FREECAD ASSEMBLY — COMPONENT RECIPES ("roommake")

This assembly document has 24 components, labeled P0..P23 below (a component is one placed body or linked part). 22 of them carry a construction recipe — the FreeCAD feature program that regenerates the part from scratch, quoted from this document or its linked companion documents; the rest are supplied as boundary geometry only. No exploded tour is included for this assembly.
NOTE — document 3 of 3 of this assembly tour. The two overview renders and the header above are repeated from document 1; the component sections below continue where the previous document stopped.
COMPONENT P19 — recipe-attached ("tv", a linked part whose construction recipe lives in a companion FreeCAD document of the same project; that document's serialized recipe follows).
Construction recipe (the companion document, serialized — sketch geometry with constraints, then the solid features built on it; lengths are millimeters unless a unit is written):

FCSTD DOCUMENT  (FreeCAD 1.0R39109 (Git))
Label: tv
License: All rights reserved
LicenseURL: https://en.wikipedia.org/wiki/All_rights_reserved
objects: Sketcher::SketchObject×9, PartDesign::Pad×6, PartDesign::Pocket×3, PartDesign::Body×3, App::Link×3, PartDesign::Fillet×2, Assembly::JointGroup×2, Assembly::AssemblyObject×2, Part::FeaturePython×2, PartDesign::ShapeBinder×2, PartDesign::Plane×2, App::Part×1
note: 60 computed .brp shape members not serialized (recipe doc carries the construction recipe); baked Part::Feature solids carry a one-line shape summary decoded from their .brp

FEATURE [Sketcher::SketchObject] Sketch003
  ArcFitTolerance = 1e-06
  AttachmentSupport = -> [XZ_Plane]
  FullyConstrained = true
  MakeInternals = false
  MapMode = 5
  Placement = pos=(0,0,0) rot=(1,0,0;1.5708rad)
  sketch-geometry (5):
    g0: LineSegment StartX=-4820 StartY=820 StartZ=0 EndX=4820 EndY=820 EndZ=0
    g1: LineSegment StartX=4820 StartY=820 StartZ=0 EndX=4820 EndY=6290 EndZ=0
    g2: LineSegment StartX=4820 StartY=6290 StartZ=0 EndX=-4820 EndY=6290 EndZ=0
    g3: LineSegment StartX=-4820 StartY=6290 StartZ=0 EndX=-4820 EndY=820 EndZ=0
    g4: GeomPoint [constr] X=0 Y=3555 Z=0
  constraints (13):
    c: Coincident(g0,g1)
    c: Coincident(g1,g2)
    c: Coincident(g2,g3)
    c: Coincident(g3,g0)
    c: Horizontal(g0)
    c: Horizontal(g2)
    c: Vertical(g1)
    c: Vertical(g3)
    c: Symmetric(g2,g0,g4)
    c: Distance(g1,g3) = 9640
    c: PointOnObject(g4,g-2)
    c: DistanceY(g1,g1) = 5470
    c: DistanceY(g0) = 820
FEATURE [PartDesign::Pad] Pad
  Direction = (0,-1,2e-16)
  Length = 100
  Length2 = 10
  Placement = pos=(0,0,0) rot=(1,0,0;1.5708rad)
  Profile = -> Sketch003
  ReferenceAxis = -> Sketch003 [N_Axis]
  Refine = true
  Suppressed = false
  Type = 0
FEATURE [Sketcher::SketchObject] Sketch004
  ArcFitTolerance = 1e-06
  AttachmentSupport = -> [Pad]
  ExternalGeometry = -> [Pad]
  FullyConstrained = true
  MakeInternals = false
  MapMode = 5
  Placement = pos=(0,7.894e-13,0) rot=(-1,0,0;1.5708rad)
  sketch-geometry (4):
    g0: LineSegment StartX=-4820 StartY=-820 StartZ=0 EndX=-4820 EndY=-1620 EndZ=0
    g1: LineSegment StartX=-4820 StartY=-1620 StartZ=0 EndX=4820 EndY=-1620 EndZ=0
    g2: LineSegment StartX=4820 StartY=-1620 StartZ=0 EndX=4820 EndY=-820 EndZ=0
    g3: LineSegment StartX=4820 StartY=-820 StartZ=0 EndX=-4820 EndY=-820 EndZ=0
  constraints (10):
    c: Coincident(g0,g1)
    c: Coincident(g1,g2)
    c: Coincident(g2,g3)
    c: Coincident(g3,g0)
    c: Vertical(g0)
    c: Vertical(g2)
    c: Horizontal(g1)
    c: DistanceY(g0,g0) = 800
    c: Coincident(g2,g-3)
    c: Coincident(g0,g-4)
FEATURE [PartDesign::Pad] Pad001
  BaseFeature = -> Pad
  Direction = (0,1,2e-16)
  Length = 800
  Length2 = 10
  Placement = pos=(0,0,0) rot=(1,0,0;1.5708rad)
  Profile = -> Sketch004
  ReferenceAxis = -> Sketch004 [N_Axis]
  Refine = true
  Suppressed = false
  Type = 0
FEATURE [Sketcher::SketchObject] Sketch005
  ArcFitTolerance = 1e-06
  AttachmentSupport = -> [Pad001]
  ExternalGeometry = -> [Pad001]
  FullyConstrained = false
  MakeInternals = false
  MapMode = 5
  Placement = pos=(0,7.894e-13,0) rot=(-1,0,0;1.5708rad)
  sketch-geometry (4):
    g0: LineSegment StartX=-4720 StartY=-6190 StartZ=0 EndX=4720 EndY=-6190 EndZ=0
    g1: LineSegment StartX=4720 StartY=-6190 StartZ=0 EndX=4720 EndY=-963.315 EndZ=0
    g2: LineSegment StartX=4720 StartY=-963.315 StartZ=0 EndX=-4720 EndY=-963.315 EndZ=0
    g3: LineSegment StartX=-4720 StartY=-963.315 StartZ=0 EndX=-4720 EndY=-6190 EndZ=0
  constraints (11):
    c: Coincident(g0,g1)
    c: Coincident(g1,g2)
    c: Coincident(g2,g3)
    c: Coincident(g3,g0)
    c: Horizontal(g0)
    c: Horizontal(g2)
    c: Vertical(g1)
    c: Vertical(g3)
    c: DistanceY(g-3,g0) = 100
    c: DistanceX(g-3,g0) = 100
    c: DistanceX(g0,g-4) = 100
FEATURE [PartDesign::Pad] Pad002
  BaseFeature = -> Pad001
  Direction = (0,1,2e-16)
  Length = 400
  Length2 = 10
  Placement = pos=(0,0,0) rot=(1,0,0;1.5708rad)
  Profile = -> Sketch005
  ReferenceAxis = -> Sketch005 [N_Axis]
  Refine = true
  Suppressed = false
  TaperAngle = -45
  Type = 0
FEATURE [Sketcher::SketchObject] Sketch008
  ArcFitTolerance = 1e-06
  AttachmentSupport = -> [Pad002]
  ExternalGeometry = -> [Pad002]
  FullyConstrained = false
  MakeInternals = false
  MapMode = 5
  Placement = pos=(0,0,1620) rot=(0,0,1;3.14159rad)
  sketch-geometry (18):
    g0: LineSegment StartX=0 StartY=-400 StartZ=0 EndX=-4226.42 EndY=-400 EndZ=0
    g1: Circle [constr] CenterX=-4226.42 CenterY=-400 CenterZ=0 NormalX=0 NormalY=0 NormalZ=1 AngleXU=0 Radius=1
    g2: Circle [constr] CenterX=-3745.48 CenterY=-741.541 CenterZ=0 NormalX=0 NormalY=0 NormalZ=1 AngleXU=0 Radius=1
    g3: Circle [constr] CenterX=-3483.42 CenterY=-773.588 CenterZ=0 NormalX=0 NormalY=0 NormalZ=1 AngleXU=0 Radius=1
    g4: BSplineCurve PolesCount=4 KnotsCount=2 Degree=3 IsPeriodic=0
    g5: GeomPoint [constr] X=-4226.42 Y=-400 Z=0
    g6: GeomPoint [constr] X=-3109.89 Y=-800 Z=0
    g7: Circle [constr] CenterX=-3109.89 CenterY=-800 CenterZ=0 NormalX=0 NormalY=0 NormalZ=1 AngleXU=0 Radius=1
    g8: LineSegment StartX=-3109.89 StartY=-800 StartZ=0 EndX=0 EndY=-800 EndZ=0
    g9: Circle [constr] CenterX=4226.42 CenterY=-400 CenterZ=0 NormalX=0 NormalY=0 NormalZ=1 AngleXU=0 Radius=1
    g10: Circle [constr] CenterX=3745.48 CenterY=-741.541 CenterZ=0 NormalX=0 NormalY=0 NormalZ=1 AngleXU=0 Radius=1
    g11: Circle [constr] CenterX=3483.42 CenterY=-773.588 CenterZ=0 NormalX=0 NormalY=0 NormalZ=1 AngleXU=0 Radius=1
    g12: BSplineCurve PolesCount=4 KnotsCount=2 Degree=3 IsPeriodic=0
    g13: GeomPoint [constr] X=4226.42 Y=-400 Z=0
    g14: GeomPoint [constr] X=3109.89 Y=-800 Z=0
    g15: Circle [constr] CenterX=3109.89 CenterY=-800 CenterZ=0 NormalX=0 NormalY=0 NormalZ=1 AngleXU=0 Radius=1
    g16: LineSegment StartX=3109.89 StartY=-800 StartZ=0 EndX=0 EndY=-800 EndZ=0
    g17: LineSegment StartX=0 StartY=-400 StartZ=0 EndX=4226.42 EndY=-400 EndZ=0
  constraints (25):
    c: Horizontal(g0)
    c: PointOnObject(g0,g-3)
    c: Weight(g1) = 1
    c: Equal(g1,g2)
    c: Equal(g1,g3)
    c: InternalAlignment(g1,g4)
    c: InternalAlignment(g2,g4)
    c: InternalAlignment(g3,g4)
    c: InternalAlignment(g5,g4)
    c: InternalAlignment(g6,g4)
    c: Coincident(g1,g0)
    c: InternalAlignment(g7,g4)
    c: Equal(g7,g1)
    c: Horizontal(g17)
    c: Weight(g9) = 1
    c: Equal(g9,g10)
    c: Equal(g9,g11)
    c: InternalAlignment(g9,g12)
    c: InternalAlignment(g10,g12)
    c: InternalAlignment(g11,g12)
    c: InternalAlignment(g13,g12)
    c: InternalAlignment(g14,g12)
    c: Coincident(g9,g17)
    c: InternalAlignment(g15,g12)
    c: Equal(g15,g9)
FEATURE [PartDesign::Pad] Pad003
  BaseFeature = -> Pad002
  Direction = (0,0,1)
  Length = 2500
  Length2 = 10
  Placement = pos=(0,0,0) rot=(1,0,0;1.5708rad)
  Profile = -> Sketch008
  ReferenceAxis = -> Sketch008 [N_Axis]
  Refine = true
  Suppressed = false
  Type = 0
FEATURE [Sketcher::SketchObject] Sketch009
  ArcFitTolerance = 1e-06
  AttachmentSupport = -> [Pad003]
  ExternalGeometry = -> [Pad003]
  FullyConstrained = false
  MakeInternals = false
  MapMode = 5
  Placement = pos=(4820,-4.5308e-12,0) rot=(0.707107,0,0.707107;3.14159rad)
  sketch-geometry (8):
    g0: LineSegment StartX=4120 StartY=-800 StartZ=0 EndX=3674.07 EndY=-800 EndZ=0
    g1: Circle [constr] CenterX=4120 CenterY=-400 CenterZ=0 NormalX=0 NormalY=0 NormalZ=1 AngleXU=0 Radius=1
    g2: Circle [constr] CenterX=3794.85 CenterY=-604.641 CenterZ=0 NormalX=0 NormalY=0 NormalZ=1 AngleXU=0 Radius=1
    g3: Circle [constr] CenterX=3674.07 CenterY=-800 CenterZ=0 NormalX=0 NormalY=0 NormalZ=1 AngleXU=0 Radius=1
    g4: BSplineCurve PolesCount=3 KnotsCount=2 Degree=2 IsPeriodic=0
    g5: GeomPoint [constr] X=4120 Y=-400 Z=0
    g6: GeomPoint [constr] X=3674.07 Y=-800 Z=0
    g7: LineSegment StartX=4120 StartY=-400 StartZ=0 EndX=4120 EndY=-800 EndZ=0
  constraints (12):
    c: Coincident(g0,g-4)
    c: Horizontal(g0)
    c: Weight(g1) = 1
    c: Equal(g1,g2)
    c: Equal(g1,g3)
    c: InternalAlignment(g1,g4)
    c: InternalAlignment(g2,g4)
    c: InternalAlignment(g3,g4)
    c: InternalAlignment(g5,g4)
    c: InternalAlignment(g6,g4)
    c: Coincident(g1,g-4)
    c: Coincident(g3,g0)
FEATURE [PartDesign::Pocket] Pocket
  BaseFeature = -> Pad003
  Direction = (-1,0,2e-16)
  Length = 5
  Length2 = 5
  Placement = pos=(0,0,0) rot=(1,0,0;1.5708rad)
  Profile = -> Sketch009
  ReferenceAxis = -> Sketch009 [N_Axis]
  Refine = true
  Suppressed = false
  Type = 1
FEATURE [Sketcher::SketchObject] Sketch010
  ArcFitTolerance = 1e-06
  AttachmentSupport = -> [Pocket]
  ExternalGeometry = -> [Pocket]
  FullyConstrained = false
  MakeInternals = false
  MapMode = 5
  Placement = pos=(0,800,0) rot=(-1,0,0;1.5708rad)
  sketch-geometry (13):
    g0: LineSegment StartX=4524.01 StartY=-3554.92 StartZ=0 EndX=4524.01 EndY=-1739.15 EndZ=0
    g1: LineSegment StartX=4524.01 StartY=-1739.15 StartZ=0 EndX=3287.44 EndY=-1739.15 EndZ=0
    g2: LineSegment StartX=3287.44 StartY=-1739.15 StartZ=0 EndX=3287.44 EndY=-3554.92 EndZ=0
    g3: LineSegment StartX=3287.44 StartY=-3554.92 StartZ=0 EndX=4524.01 EndY=-3554.92 EndZ=0
    g4: LineSegment StartX=-3287.44 StartY=-2395.51 StartZ=0 EndX=-3287.44 EndY=-1732.57 EndZ=0
    g5: LineSegment StartX=-3287.44 StartY=-1732.57 StartZ=0 EndX=-4524.01 EndY=-1732.57 EndZ=0
    g6: LineSegment StartX=-4524.01 StartY=-1732.57 StartZ=0 EndX=-4524.01 EndY=-2395.51 EndZ=0
    g7: LineSegment StartX=-4524.01 StartY=-2395.51 StartZ=0 EndX=-3287.44 EndY=-2395.51 EndZ=0
    g8: LineSegment [constr] StartX=3287.44 StartY=-3554.92 StartZ=0 EndX=3109.89 EndY=-3554.92 EndZ=0
    g9: LineSegment [constr] StartX=3109.89 StartY=-3554.92 StartZ=0 EndX=3109.89 EndY=-3674.07 EndZ=0
    g10: LineSegment [constr] StartX=3287.44 StartY=-1739.15 StartZ=0 EndX=3109.89 EndY=-1739.15 EndZ=0
    g11: LineSegment [constr] StartX=3109.89 StartY=-1739.15 StartZ=0 EndX=3109.89 EndY=-1620 EndZ=0
    g12: LineSegment [constr] StartX=-3287.44 StartY=-1732.57 StartZ=0 EndX=-3109.89 EndY=-1732.57 EndZ=0
  constraints (32):
    c: Coincident(g0,g1)
    c: Coincident(g1,g2)
    c: Coincident(g2,g3)
    c: Coincident(g3,g0)
    c: Vertical(g0)
    c: Vertical(g2)
    c: Horizontal(g1)
    c: Horizontal(g3)
    c: Coincident(g4,g5)
    c: Coincident(g5,g6)
    c: Coincident(g6,g7)
    c: Coincident(g7,g4)
    c: Vertical(g4)
    c: Vertical(g6)
    c: Horizontal(g5)
    c: Horizontal(g7)
    c: Coincident(g8,g2)
    c: PointOnObject(g8,g-3)
    c: Horizontal(g8)
    c: Coincident(g9,g8)
    c: Coincident(g9,g-3)
    c: Coincident(g10,g1)
    c: PointOnObject(g10,g-3)
    c: Horizontal(g10)
    c: Coincident(g11,g10)
    c: Coincident(g11,g-3)
    c: Equal(g9,g11)
    c: Coincident(g12,g4)
    c: PointOnObject(g12,g-4)
    c: Horizontal(g12)
    c: Equal(g12,g10)
    c: Equal(g3,g7)
FEATURE [PartDesign::Pocket] Pocket001
  BaseFeature = -> Pocket
  Direction = (0,-1,-2e-16)
  Length = 330
  Length2 = 5
  Placement = pos=(0,0,0) rot=(1,0,0;1.5708rad)
  Profile = -> Sketch010
  ReferenceAxis = -> Sketch010 [N_Axis]
  Refine = true
  Suppressed = false
  Type = 0
FEATURE [PartDesign::Fillet] Fillet
  Base = -> Pocket001 [Edge54,Edge57]
  BaseFeature = -> Pocket001
  Placement = pos=(0,0,0) rot=(1,0,0;1.5708rad)
  Radius = 50
  Refine = true
  SupportTransform = false
  Suppressed = false
  UseAllEdges = false
FEATURE [PartDesign::Fillet] Fillet001
  Base = -> Fillet [Edge16,Edge1,Edge62,Edge64]
  BaseFeature = -> Fillet
  Placement = pos=(0,0,0) rot=(1,0,0;1.5708rad)
  Radius = 50
  Refine = true
  SupportTransform = false
  Suppressed = false
  UseAllEdges = false
FEATURE [Sketcher::SketchObject] Sketch011
  ArcFitTolerance = 1e-06
  AttachmentSupport = -> [Fillet001]
  ExternalGeometry = -> [Fillet001]
  FullyConstrained = true
  MakeInternals = false
  MapMode = 5
  Placement = pos=(0,-100,0) rot=(1,0,0;1.5708rad)
  sketch-geometry (4):
    g0: LineSegment StartX=-4807.8 StartY=6277.8 StartZ=0 EndX=-4807.8 EndY=832.2 EndZ=0
    g1: LineSegment StartX=-4807.8 StartY=832.2 StartZ=0 EndX=4807.8 EndY=832.2 EndZ=0
    g2: LineSegment StartX=4807.8 StartY=832.2 StartZ=0 EndX=4807.8 EndY=6277.8 EndZ=0
    g3: LineSegment StartX=4807.8 StartY=6277.8 StartZ=0 EndX=-4807.8 EndY=6277.8 EndZ=0
  constraints (12):
    c: Coincident(g0,g1)
    c: Coincident(g1,g2)
    c: Coincident(g2,g3)
    c: Coincident(g3,g0)
    c: Vertical(g0)
    c: Vertical(g2)
    c: Horizontal(g1)
    c: Horizontal(g3)
    c: DistanceY(g0,g-3) = 12.2
    c: DistanceX(g-3,g0) = 12.2
    c: DistanceX(g1,g-4) = 12.2
    c: DistanceY(g-4,g1) = 12.2
FEATURE [PartDesign::Pocket] Pocket002
  BaseFeature = -> Fillet001
  Direction = (0,1,-2e-16)
  Length = 2
  Length2 = 5
  Placement = pos=(0,0,0) rot=(1,0,0;1.5708rad)
  Profile = -> Sketch011
  ReferenceAxis = -> Sketch011 [N_Axis]
  Refine = true
  Suppressed = false
  Type = 0
FEATURE [PartDesign::Body] Body
  AllowCompound = false
  Group = -> [Sketch003,Pad,Sketch004,Pad001,Sketch005,Pad002,Sketch008,Pad003,Sketch009,Pocket,Sketch010,Pocket001,Fillet,Fillet001,Sketch011,Pocket002]
  Origin = -> Origin
  Tip = -> Pocket002
FEATURE [Assembly::JointGroup] Joints
FEATURE [App::Link] Body003  label="Screen"
  LinkPlacement = pos=(0,-350,0) rot=(0,0,1;0rad)
  LinkedObject = -> Body
  Placement = pos=(0,-350,0) rot=(0,0,1;0rad)
FEATURE [Assembly::AssemblyObject] Assembly  label="Screen_a"
  Group = -> [Joints,Body003]
  Origin = -> Origin003
  Placement = pos=(0,-350,0) rot=(0,0,1;0rad)
  Type = Assembly
FEATURE [Part::FeaturePython] Clone001  label="Screen_clone"  # Draft clone (typed FeaturePython)
  AttacherType = Attacher::AttachEngine3D
  Fuse = false
  Objects = -> [Assembly]
  Scale = (0.1,0.1,0.1)
FEATURE [Assembly::JointGroup] Joints001
FEATURE [PartDesign::ShapeBinder] CopyFillet001
  Placement = pos=(0,0,0) rot=(1,0,0;1.5708rad)
  TraceSupport = false
FEATURE [PartDesign::Plane] DatumPlane
  AttachmentOffset = pos=(0,0,-1500) rot=(0,0,1;0rad)
  AttachmentSupport = -> [CopyFillet001]
  Length = 6989.3
  MapMode = 5
  Placement = pos=(3320,0,3.331e-13) rot=(0.707107,0,0.707107;3.14159rad)
  ResizeMode = 0
  Width = 2474.3
FEATURE [Sketcher::SketchObject] Sketch006
  ArcFitTolerance = 1e-06
  AttachmentSupport = -> [DatumPlane]
  ExternalGeometry = -> [CopyFillet001]
  FullyConstrained = false
  MakeInternals = false
  MapMode = 5
  Placement = pos=(3320,0,3.331e-13) rot=(0.707107,0,0.707107;3.14159rad)
  sketch-geometry (17):
    g0: LineSegment StartX=820 StartY=-119.068 StartZ=0 EndX=820 EndY=-580.932 EndZ=0
    g1: LineSegment StartX=820 StartY=-119.068 StartZ=0 EndX=736.366 EndY=-119.068 EndZ=0
    g2: LineSegment StartX=820 StartY=-580.932 StartZ=0 EndX=742.416 EndY=-580.932 EndZ=0
    g3: LineSegment StartX=680.048 StartY=-96.5682 StartZ=0 EndX=0 EndY=550 EndZ=0
    g4: LineSegment StartX=686.36 StartY=-603.183 StartZ=0 EndX=0 EndY=-1250 EndZ=0
    g5: LineSegment [constr] StartX=820 StartY=-350 StartZ=0 EndX=0 EndY=-350 EndZ=0
    g6: LineSegment [constr] StartX=820 StartY=100 StartZ=0 EndX=820 EndY=-119.068 EndZ=0
    g7: LineSegment [constr] StartX=820 StartY=-580.932 StartZ=0 EndX=820 EndY=-800 EndZ=0
    g8: LineSegment StartX=0 StartY=408.983 StartZ=0 EndX=671.046 EndY=-229.026 EndZ=0
    g9: LineSegment StartX=670.497 StartY=-477.115 StartZ=0 EndX=0 EndY=-1108.98 EndZ=0
    g10: ArcOfCircle CenterX=553.355 CenterY=-352.811 CenterZ=0 NormalX=0 NormalY=0 NormalZ=1 AngleXU=0 Radius=170.803 StartAngle=5.46813 EndAngle=7.09382
    g11: LineSegment StartX=0 StartY=550 StartZ=0 EndX=0 EndY=408.983 EndZ=0
    g12: LineSegment StartX=0 StartY=-1108.98 StartZ=0 EndX=0 EndY=-1250 EndZ=0
    g13: ArcOfCircle CenterX=736.366 CenterY=-37.3338 CenterZ=0 NormalX=0 NormalY=0 NormalZ=1 AngleXU=0 Radius=81.7339 StartAngle=3.95222 EndAngle=4.71239
    g14: GeomPoint [constr] X=703.713 Y=-119.068 Z=0
    g15: ArcOfCircle CenterX=742.416 CenterY=-662.666 CenterZ=0 NormalX=0 NormalY=0 NormalZ=1 AngleXU=0 Radius=81.7339 StartAngle=1.5708 EndAngle=2.32654
    g16: GeomPoint [constr] X=709.972 Y=-580.932 Z=0
  constraints (37):
    c: PointOnObject(g0,g-3)
    c: PointOnObject(g0,g-3)
    c: Coincident(g1,g0)
    c: Horizontal(g1)
    c: Coincident(g2,g0)
    c: Horizontal(g2)
    c: PointOnObject(g3,g-2)
    c: DistanceY(g4,g3) = 1800
    c: PointOnObject(g4,g-2)
    c: Symmetric(g0,g0,g5)
    c: Horizontal(g5)
    c: Symmetric(g4,g3,g5)
    c: Coincident(g6,g-3)
    c: Coincident(g6,g0)
    c: Coincident(g7,g0)
    c: Coincident(g7,g-3)
    c: Equal(g7,g6)
    c: PointOnObject(g8,g-2)
    c: PointOnObject(g9,g-2)
    c: Parallel(g8,g3)
    c: Parallel(g9,g4)
    c: Tangent(g8,g10) = 1.5708
    c: Tangent(g9,g10) = 1.5708
    c: Coincident(g11,g3)
    c: Coincident(g11,g8)
    c: Coincident(g12,g9)
    c: Coincident(g12,g4)
    c: PointOnObject(g14,g1)
    c: PointOnObject(g14,g3)
    c: Tangent(g1,g13) = 1.5708
    c: Tangent(g3,g13) = 1.5708
    c: PointOnObject(g16,g2)
    c: PointOnObject(g16,g4)
    c: Tangent(g2,g15) = -1.5708
    c: Tangent(g4,g15) = -1.5708
    c: Equal(g13,g15)
    c: Equal(g12,g11)
FEATURE [PartDesign::Pad] Pad004
  Direction = (1,0,-2e-16)
  Length = 200
  Length2 = 10
  Placement = pos=(3320,0,3.331e-13) rot=(0.707107,0,0.707107;3.14159rad)
  Profile = -> Sketch006
  ReferenceAxis = -> Sketch006 [N_Axis]
  Refine = true
  Reversed = true
  Suppressed = false
  Type = 0
FEATURE [PartDesign::Body] Body001
  AllowCompound = false
  Group = -> [DatumPlane,CopyFillet001,Sketch006,Pad004]
  Origin = -> Origin001
  Tip = -> Pad004
FEATURE [App::Link] Body004  label="Right_Stand"
  LinkPlacement = pos=(0,-350,0) rot=(0,0,1;0rad)
  LinkedObject = -> Body001
  Placement = pos=(0,-350,0) rot=(0,0,1;0rad)
FEATURE [PartDesign::ShapeBinder] CopyFillet002
  Placement = pos=(0,0,0) rot=(1,0,0;1.5708rad)
  TraceSupport = false
FEATURE [PartDesign::Plane] DatumPlane001
  AttachmentOffset = pos=(0,0,-1500) rot=(0,0,1;0rad)
  AttachmentSupport = -> [CopyFillet002]
  Length = 6989.3
  MapMode = 5
  Placement = pos=(-3320,0,3.331e-13) rot=(0.707107,0,-0.707107;3.14159rad)
  ResizeMode = 0
  Width = 2474.3
FEATURE [Sketcher::SketchObject] Sketch007
  ArcFitTolerance = 1e-06
  AttachmentSupport = -> [DatumPlane001]
  FullyConstrained = false
  MakeInternals = false
  MapMode = 5
  Placement = pos=(-3320,0,3.331e-13) rot=(0.707107,0,-0.707107;3.14159rad)
  sketch-geometry (17):
    g0: LineSegment StartX=-820 StartY=-580.932 StartZ=0 EndX=-820 EndY=-119.068 EndZ=0
    g1: LineSegment StartX=-820 StartY=-580.932 StartZ=0 EndX=-736.366 EndY=-580.932 EndZ=0
    g2: LineSegment StartX=-820 StartY=-119.068 StartZ=0 EndX=-742.416 EndY=-119.068 EndZ=0
    g3: LineSegment StartX=-680.048 StartY=-603.432 StartZ=0 EndX=0 EndY=-1250 EndZ=0
    g4: LineSegment StartX=-686.36 StartY=-96.8166 StartZ=0 EndX=0 EndY=550 EndZ=0
    g5: LineSegment [constr] StartX=-820 StartY=-350 StartZ=0 EndX=0 EndY=-350 EndZ=0
    g6: LineSegment [constr] StartX=-820 StartY=-800 StartZ=0 EndX=-820 EndY=-580.932 EndZ=0
    g7: LineSegment [constr] StartX=-820 StartY=-119.068 StartZ=0 EndX=-820 EndY=100 EndZ=0
    g8: LineSegment StartX=0 StartY=-1108.98 StartZ=0 EndX=-671.046 EndY=-470.974 EndZ=0
    g9: LineSegment StartX=-670.497 StartY=-222.885 StartZ=0 EndX=0 EndY=408.983 EndZ=0
    g10: ArcOfCircle CenterX=-553.355 CenterY=-347.189 CenterZ=0 NormalX=0 NormalY=0 NormalZ=1 AngleXU=0 Radius=170.803 StartAngle=2.32654 EndAngle=3.95222
    g11: LineSegment StartX=0 StartY=-1250 StartZ=0 EndX=0 EndY=-1108.98 EndZ=0
    g12: LineSegment StartX=0 StartY=408.983 StartZ=0 EndX=0 EndY=550 EndZ=0
    g13: ArcOfCircle CenterX=-736.366 CenterY=-662.666 CenterZ=0 NormalX=0 NormalY=0 NormalZ=1 AngleXU=0 Radius=81.734 StartAngle=0.81063 EndAngle=1.5708
    g14: GeomPoint [constr] X=-703.713 Y=-580.932 Z=0
    g15: ArcOfCircle CenterX=-742.416 CenterY=-37.3338 CenterZ=0 NormalX=0 NormalY=0 NormalZ=1 AngleXU=0 Radius=81.734 StartAngle=4.71239 EndAngle=5.46813
    g16: GeomPoint [constr] X=-709.972 Y=-119.068 Z=0
  constraints (25):
    c: Coincident(g1,g0)
    c: Coincident(g2,g0)
    c: Symmetric(g0,g0,g5)
    c: Symmetric(g4,g3,g5)
    c: Coincident(g6,g0)
    c: Coincident(g7,g0)
    c: Equal(g7,g6)
    c: Parallel(g8,g3)
    c: Parallel(g9,g4)
    c: Tangent(g8,g10) = 1.5708
    c: Tangent(g9,g10) = 1.5708
    c: Coincident(g11,g3)
    c: Coincident(g11,g8)
    c: Coincident(g12,g9)
    c: Coincident(g12,g4)
    c: PointOnObject(g14,g1)
    c: PointOnObject(g14,g3)
    c: Tangent(g1,g13) = 1.5708
    c: Tangent(g3,g13) = 1.5708
    c: PointOnObject(g16,g2)
    c: PointOnObject(g16,g4)
    c: Tangent(g2,g15) = -1.5708
    c: Tangent(g4,g15) = -1.5708
    c: Equal(g13,g15)
    c: Equal(g12,g11)
FEATURE [PartDesign::Pad] Pad005
  Direction = (-1,0,-2e-16)
  Length = 200
  Length2 = 10
  Placement = pos=(-3320,0,3.331e-13) rot=(0.707107,0,-0.707107;3.14159rad)
  Profile = -> Sketch007
  ReferenceAxis = -> Sketch007 [N_Axis]
  Refine = true
  Reversed = true
  Suppressed = false
  Type = 0
FEATURE [PartDesign::Body] Body002
  AllowCompound = false
  Group = -> [DatumPlane001,CopyFillet002,Sketch007,Pad005]
  Origin = -> Origin002
  Tip = -> Pad005
FEATURE [App::Link] Body005  label="Left_Stand"
  LinkPlacement = pos=(0,-350,0) rot=(0,0,1;0rad)
  LinkedObject = -> Body002
  Placement = pos=(0,-350,0) rot=(0,0,1;0rad)
FEATURE [Assembly::AssemblyObject] Assembly001  label="Stand_a"
  Group = -> [Joints001,Body004,Body005]
  Origin = -> Origin005
  Placement = pos=(0,-350,0) rot=(0,0,1;0rad)
  Type = Assembly
FEATURE [Part::FeaturePython] Clone  label="Stand_clone"  # Draft clone (typed FeaturePython)
  AttacherType = Attacher::AttachEngine3D
  Fuse = false
  Objects = -> [Assembly001]
  Scale = (0.1,0.1,0.1)
FEATURE [App::Part] Part001  label="tv"
  Group = -> [Clone001,Clone]
  Origin = -> Origin004
COMPONENT P20 — recipe-attached ("tvboard", a linked part whose construction recipe lives in a companion FreeCAD document of the same project; that document's serialized recipe follows).
Construction recipe (the companion document, serialized — sketch geometry with constraints, then the solid features built on it; lengths are millimeters unless a unit is written):

FCSTD DOCUMENT  (FreeCAD 1.0R39109 (Git))
Label: tvboard
License: All rights reserved
LicenseURL: https://en.wikipedia.org/wiki/All_rights_reserved
objects: Sketcher::SketchObject×9, PartDesign::Pad×8, PartDesign::Plane×1, PartDesign::Pocket×1, PartDesign::Body×1, Part::FeaturePython×1, App::Part×1
note: 48 computed .brp shape members not serialized (recipe doc carries the construction recipe); baked Part::Feature solids carry a one-line shape summary decoded from their .brp

FEATURE [Sketcher::SketchObject] Sketch
  ArcFitTolerance = 1e-06
  AttachmentSupport = -> [XY_Plane]
  FullyConstrained = true
  MakeInternals = false
  MapMode = 5
  sketch-geometry (5):
    g0: LineSegment StartX=-542.5 StartY=-140 StartZ=0 EndX=542.5 EndY=-140 EndZ=0
    g1: LineSegment StartX=542.5 StartY=-140 StartZ=0 EndX=542.5 EndY=140 EndZ=0
    g2: LineSegment StartX=542.5 StartY=140 StartZ=0 EndX=-542.5 EndY=140 EndZ=0
    g3: LineSegment StartX=-542.5 StartY=140 StartZ=0 EndX=-542.5 EndY=-140 EndZ=0
    g4: GeomPoint [constr] X=0 Y=0 Z=0
  constraints (12):
    c: Coincident(g0,g1)
    c: Coincident(g1,g2)
    c: Coincident(g2,g3)
    c: Coincident(g3,g0)
    c: Horizontal(g0)
    c: Horizontal(g2)
    c: Vertical(g1)
    c: Vertical(g3)
    c: Symmetric(g2,g0,g4)
    c: Distance(g1,g3) = 1085
    c: Distance(g0,g2) = 280
    c: Coincident(g4,g-1)
FEATURE [PartDesign::Pad] Pad
  Direction = (0,0,1)
  Length = 50
  Length2 = 10
  Profile = -> Sketch
  ReferenceAxis = -> Sketch [N_Axis]
  Refine = true
  Suppressed = false
  Type = 0
FEATURE [Sketcher::SketchObject] Sketch001
  ArcFitTolerance = 1e-06
  AttachmentSupport = -> [Pad]
  FullyConstrained = true
  MakeInternals = false
  MapMode = 5
  Placement = pos=(0,0,50) rot=(0,0,1;0rad)
  sketch-geometry (5):
    g0: LineSegment StartX=-550 StartY=-147.5 StartZ=0 EndX=550 EndY=-147.5 EndZ=0
    g1: LineSegment StartX=550 StartY=-147.5 StartZ=0 EndX=550 EndY=147.5 EndZ=0
    g2: LineSegment StartX=550 StartY=147.5 StartZ=0 EndX=-550 EndY=147.5 EndZ=0
    g3: LineSegment StartX=-550 StartY=147.5 StartZ=0 EndX=-550 EndY=-147.5 EndZ=0
    g4: GeomPoint [constr] X=0 Y=0 Z=0
  constraints (12):
    c: Coincident(g0,g1)
    c: Coincident(g1,g2)
    c: Coincident(g2,g3)
    c: Coincident(g3,g0)
    c: Horizontal(g0)
    c: Horizontal(g2)
    c: Vertical(g1)
    c: Vertical(g3)
    c: Symmetric(g2,g0,g4)
    c: Distance(g1,g3) = 1100
    c: Distance(g0,g2) = 295
    c: Coincident(g4,g-1)
FEATURE [PartDesign::Pad] Pad001
  BaseFeature = -> Pad
  Direction = (0,0,1)
  Length = 10
  Length2 = 10
  Profile = -> Sketch001
  ReferenceAxis = -> Sketch001 [N_Axis]
  Refine = true
  Suppressed = false
  Type = 0
FEATURE [Sketcher::SketchObject] Sketch002
  ArcFitTolerance = 1e-06
  AttachmentSupport = -> [Pad001]
  ExternalGeometry = -> [Pad001]
  FullyConstrained = false
  MakeInternals = false
  MapMode = 5
  Placement = pos=(0,0,60) rot=(0,0,1;0rad)
  sketch-geometry (16):
    g0: LineSegment StartX=-549 StartY=146.5 StartZ=0 EndX=-549 EndY=-135.5 EndZ=0
    g1: LineSegment StartX=-549 StartY=-135.5 StartZ=0 EndX=-539 EndY=-135.5 EndZ=0
    g2: LineSegment StartX=-539 StartY=-135.5 StartZ=0 EndX=-539 EndY=146.5 EndZ=0
    g3: LineSegment StartX=-539 StartY=146.5 StartZ=0 EndX=-549 EndY=146.5 EndZ=0
    g4: LineSegment StartX=-260 StartY=146.5 StartZ=0 EndX=-260 EndY=-135.5 EndZ=0
    g5: LineSegment StartX=-260 StartY=-135.5 StartZ=0 EndX=-250 EndY=-135.5 EndZ=0
    g6: LineSegment StartX=-250 StartY=-135.5 StartZ=0 EndX=-250 EndY=146.5 EndZ=0
    g7: LineSegment StartX=-250 StartY=146.5 StartZ=0 EndX=-260 EndY=146.5 EndZ=0
    g8: LineSegment StartX=250 StartY=146.5 StartZ=0 EndX=250 EndY=-135.5 EndZ=0
    g9: LineSegment StartX=250 StartY=-135.5 StartZ=0 EndX=260 EndY=-135.5 EndZ=0
    g10: LineSegment StartX=260 StartY=-135.5 StartZ=0 EndX=260 EndY=146.5 EndZ=0
    g11: LineSegment StartX=260 StartY=146.5 StartZ=0 EndX=250 EndY=146.5 EndZ=0
    g12: LineSegment StartX=549 StartY=146.5 StartZ=0 EndX=549 EndY=-135.5 EndZ=0
    g13: LineSegment StartX=549 StartY=-135.5 StartZ=0 EndX=539 EndY=-135.5 EndZ=0
    g14: LineSegment StartX=539 StartY=-135.5 StartZ=0 EndX=539 EndY=146.5 EndZ=0
    g15: LineSegment StartX=539 StartY=146.5 StartZ=0 EndX=549 EndY=146.5 EndZ=0
  constraints (43):
    c: Coincident(g0,g1)
    c: Coincident(g1,g2)
    c: Coincident(g2,g3)
    c: Coincident(g3,g0)
    c: Vertical(g0)
    c: Vertical(g2)
    c: Horizontal(g1)
    c: Horizontal(g3)
    c: DistanceY(g0,g-4) = 1
    c: DistanceX(g-4,g0) = 1
    c: DistanceX(g3,g3) = 10
    c: DistanceY(g-3,g1) = 12
    c: Coincident(g4,g5)
    c: Coincident(g5,g6)
    c: Coincident(g6,g7)
    c: Coincident(g7,g4)
    c: Vertical(g4)
    c: Vertical(g6)
    c: Horizontal(g5)
    c: Horizontal(g7)
    c: Coincident(g8,g9)
    c: Coincident(g9,g10)
    c: Coincident(g10,g11)
    c: Coincident(g11,g8)
    c: Vertical(g8)
    c: Vertical(g10)
    c: Horizontal(g9)
    c: Horizontal(g11)
    c: Symmetric(g5,g8,g-2)
    c: DistanceX(g5,g8) = 500
    c: Equal(g7,g11)
    c: Equal(g11,g3)
    c: Horizontal(g4,g8)
    c: Horizontal(g8,g2)
    c: Horizontal(g4,g1)
    c: Coincident(g12,g13)
    c: Coincident(g13,g14)
    c: Coincident(g14,g15)
    c: Coincident(g15,g12)
    c: Vertical(g12)
    c: Vertical(g14)
    c: Horizontal(g13)
    c: Horizontal(g15)
FEATURE [PartDesign::Pad] Pad002
  BaseFeature = -> Pad001
  Direction = (0,0,1)
  Length = 250
  Length2 = 10
  Profile = -> Sketch002
  ReferenceAxis = -> Sketch002 [N_Axis]
  Refine = true
  Suppressed = false
  Type = 0
FEATURE [PartDesign::Plane] DatumPlane
  AttachmentOffset = pos=(0,0,1) rot=(0,0,1;0rad)
  AttachmentSupport = -> [Pad002]
  Length = 60
  MapMode = 5
  Placement = pos=(0,0,61) rot=(0,0,1;0rad)
  ResizeMode = 0
  Width = 60
FEATURE [Sketcher::SketchObject] Sketch003
  ArcFitTolerance = 1e-06
  AttachmentSupport = -> [Pad002]
  ExternalGeometry = -> [Pad002]
  FullyConstrained = false
  MakeInternals = false
  MapMode = 5
  Placement = pos=(0,0,60) rot=(0,0,1;0rad)
  sketch-geometry (5):
    g0: Circle CenterX=544 CenterY=-141.5 CenterZ=0 NormalX=0 NormalY=0 NormalZ=1 AngleXU=0 Radius=2
    g1: LineSegment [constr] StartX=549 StartY=-135.5 StartZ=0 EndX=549 EndY=-147.5 EndZ=0
    g2: GeomPoint X=549 Y=-141.5 Z=0
    g3: GeomPoint X=544 Y=-135.5 Z=0
    g4: Circle CenterX=-544 CenterY=-141.5 CenterZ=0 NormalX=0 NormalY=0 NormalZ=1 AngleXU=0 Radius=2
  constraints (9):
    c: Coincident(g1,g-4)
    c: PointOnObject(g1,g-3)
    c: Vertical(g1)
    c: Symmetric(g1,g1,g2)
    c: Horizontal(g2,g0)
    c: Symmetric(g-4,g1,g3)
    c: Vertical(g3,g0)
    c: Radius(g0) = 2
    c: Radius(g4) = 2
FEATURE [PartDesign::Pad] Pad003
  BaseFeature = -> Pad002
  Direction = (0,0,1)
  Length = 250
  Length2 = 10
  Profile = -> Sketch003
  ReferenceAxis = -> Sketch003 [N_Axis]
  Refine = true
  Suppressed = false
  Type = 0
FEATURE [Sketcher::SketchObject] Sketch004
  ArcFitTolerance = 1e-06
  AttachmentSupport = -> [DatumPlane]
  ExternalGeometry = -> [Pad003]
  FullyConstrained = false
  MakeInternals = false
  MapMode = 5
  Placement = pos=(0,0,61) rot=(0,0,1;0rad)
  sketch-geometry (8):
    g0: LineSegment StartX=-549 StartY=-136.5 StartZ=0 EndX=-549 EndY=-146.5 EndZ=0
    g1: LineSegment StartX=-549 StartY=-146.5 StartZ=0 EndX=-250 EndY=-146.5 EndZ=0
    g2: LineSegment StartX=-250 StartY=-146.5 StartZ=0 EndX=-250 EndY=-136.5 EndZ=0
    g3: LineSegment StartX=-250 StartY=-136.5 StartZ=0 EndX=-549 EndY=-136.5 EndZ=0
    g4: LineSegment StartX=549 StartY=-136.5 StartZ=0 EndX=549 EndY=-146.5 EndZ=0
    g5: LineSegment StartX=549 StartY=-146.5 StartZ=0 EndX=250 EndY=-146.5 EndZ=0
    g6: LineSegment StartX=250 StartY=-146.5 StartZ=0 EndX=250 EndY=-136.5 EndZ=0
    g7: LineSegment StartX=250 StartY=-136.5 StartZ=0 EndX=549 EndY=-136.5 EndZ=0
  constraints (20):
    c: Coincident(g0,g1)
    c: Coincident(g1,g2)
    c: Coincident(g2,g3)
    c: Coincident(g3,g0)
    c: Vertical(g0)
    c: Vertical(g2)
    c: Horizontal(g1)
    c: Horizontal(g3)
    c: Vertical(g2,g-5)
    c: Vertical(g0,g-3)
    c: DistanceY(g-4,g0) = 1
    c: DistanceY(g0,g0) = 10
    c: Coincident(g4,g5)
    c: Coincident(g5,g6)
    c: Coincident(g6,g7)
    c: Coincident(g7,g4)
    c: Vertical(g4)
    c: Vertical(g6)
    c: Horizontal(g5)
    c: Horizontal(g7)
FEATURE [PartDesign::Pad] Pad004
  BaseFeature = -> Pad003
  Direction = (0,0,1)
  Length = 248
  Length2 = 10
  Profile = -> Sketch004
  ReferenceAxis = -> Sketch004 [N_Axis]
  Refine = true
  Suppressed = false
  Type = 0
FEATURE [Sketcher::SketchObject] Sketch005
  ArcFitTolerance = 1e-06
  AttachmentSupport = -> [Pad004]
  ExternalGeometry = -> [Pad004]
  FullyConstrained = true
  MakeInternals = false
  MapMode = 5
  Placement = pos=(0,-135.5,0) rot=(1,0,0;1.5708rad)
  sketch-geometry (5):
    g0: LineSegment StartX=-250 StartY=190 StartZ=0 EndX=-250 EndY=180 EndZ=0
    g1: LineSegment StartX=-250 StartY=180 StartZ=0 EndX=250 EndY=180 EndZ=0
    g2: LineSegment StartX=250 StartY=180 StartZ=0 EndX=250 EndY=190 EndZ=0
    g3: LineSegment StartX=250 StartY=190 StartZ=0 EndX=-250 EndY=190 EndZ=0
    g4: GeomPoint X=-250 Y=185 Z=0
  constraints (12):
    c: Coincident(g0,g1)
    c: Coincident(g1,g2)
    c: Coincident(g2,g3)
    c: Coincident(g3,g0)
    c: Vertical(g0)
    c: Vertical(g2)
    c: Horizontal(g1)
    c: Horizontal(g3)
    c: PointOnObject(g1,g-4)
    c: DistanceY(g2,g2) = 10
    c: Symmetric(g-3,g-3,g4)
    c: Symmetric(g0,g0,g4)
FEATURE [PartDesign::Pad] Pad005
  BaseFeature = -> Pad004
  Direction = (0,-1,2e-16)
  Length = 275
  Length2 = 10
  Profile = -> Sketch005
  ReferenceAxis = -> Sketch005 [N_Axis]
  Reversed = true
  Suppressed = false
  Type = 0
FEATURE [Sketcher::SketchObject] Sketch006
  ArcFitTolerance = 1e-06
  AttachmentSupport = -> [Pad005]
  ExternalGeometry = -> [Pad005]
  FullyConstrained = false
  MakeInternals = false
  MapMode = 5
  Placement = pos=(0,0,60) rot=(0,0,1;0rad)
  sketch-geometry (8):
    g0: LineSegment StartX=-539 StartY=146.5 StartZ=0 EndX=-539 EndY=136.5 EndZ=0
    g1: LineSegment StartX=-539 StartY=136.5 StartZ=0 EndX=-260 EndY=136.5 EndZ=0
    g2: LineSegment StartX=-260 StartY=136.5 StartZ=0 EndX=-260 EndY=146.5 EndZ=0
    g3: LineSegment StartX=-260 StartY=146.5 StartZ=0 EndX=-539 EndY=146.5 EndZ=0
    g4: LineSegment StartX=539 StartY=146.5 StartZ=0 EndX=539 EndY=136.5 EndZ=0
    g5: LineSegment StartX=539 StartY=136.5 StartZ=0 EndX=260 EndY=136.5 EndZ=0
    g6: LineSegment StartX=260 StartY=136.5 StartZ=0 EndX=260 EndY=146.5 EndZ=0
    g7: LineSegment StartX=260 StartY=146.5 StartZ=0 EndX=539 EndY=146.5 EndZ=0
  constraints (19):
    c: Coincident(g0,g1)
    c: Coincident(g1,g2)
    c: Coincident(g2,g3)
    c: Coincident(g3,g0)
    c: Vertical(g0)
    c: Vertical(g2)
    c: Horizontal(g1)
    c: Horizontal(g3)
    c: Coincident(g0,g-3)
    c: PointOnObject(g1,g-4)
    c: DistanceY(g2,g2) = 10
    c: Coincident(g4,g5)
    c: Coincident(g5,g6)
    c: Coincident(g6,g7)
    c: Coincident(g7,g4)
    c: Vertical(g4)
    c: Vertical(g6)
    c: Horizontal(g5)
    c: Horizontal(g7)
FEATURE [PartDesign::Pad] Pad006
  BaseFeature = -> Pad005
  Direction = (0,0,1)
  Length = 250
  Length2 = 10
  Profile = -> Sketch006
  ReferenceAxis = -> Sketch006 [N_Axis]
  Suppressed = false
  Type = 0
FEATURE [Sketcher::SketchObject] Sketch007
  ArcFitTolerance = 1e-06
  AttachmentSupport = -> [Pad006]
  ExternalGeometry = -> [Pad006]
  FullyConstrained = true
  MakeInternals = false
  MapMode = 5
  Placement = pos=(0,0,310) rot=(0,0,1;0rad)
  sketch-geometry (4):
    g0: LineSegment StartX=-550 StartY=147.5 StartZ=0 EndX=-550 EndY=-147.5 EndZ=0
    g1: LineSegment StartX=-550 StartY=-147.5 StartZ=0 EndX=550 EndY=-147.5 EndZ=0
    g2: LineSegment StartX=550 StartY=-147.5 StartZ=0 EndX=550 EndY=147.5 EndZ=0
    g3: LineSegment StartX=550 StartY=147.5 StartZ=0 EndX=-550 EndY=147.5 EndZ=0
  constraints (10):
    c: Coincident(g0,g1)
    c: Coincident(g1,g2)
    c: Coincident(g2,g3)
    c: Coincident(g3,g0)
    c: Vertical(g0)
    c: Vertical(g2)
    c: Horizontal(g1)
    c: Horizontal(g3)
    c: Coincident(g0,g-3)
    c: Coincident(g1,g-4)
FEATURE [PartDesign::Pad] Pad007
  BaseFeature = -> Pad006
  Direction = (0,0,1)
  Length = 10
  Length2 = 10
  Profile = -> Sketch007
  ReferenceAxis = -> Sketch007 [N_Axis]
  Suppressed = false
  Type = 0
FEATURE [Sketcher::SketchObject] Sketch008
  ArcFitTolerance = 1e-06
  AttachmentSupport = -> [Pad007]
  FullyConstrained = false
  MakeInternals = false
  MapMode = 5
  Placement = pos=(0,0,320) rot=(0,0,1;0rad)
  sketch-geometry (4):
    g0: LineSegment StartX=-99.9826 StartY=172.692 StartZ=0 EndX=99.9826 EndY=172.692 EndZ=0
    g1: LineSegment StartX=99.9826 StartY=172.692 StartZ=0 EndX=55.785 EndY=129.303 EndZ=0
    g2: LineSegment StartX=55.785 StartY=129.303 StartZ=0 EndX=-55.785 EndY=129.303 EndZ=0
    g3: LineSegment StartX=-55.785 StartY=129.303 StartZ=0 EndX=-99.9826 EndY=172.692 EndZ=0
  constraints (6):
    c: Coincident(g0,g1)
    c: Coincident(g1,g2)
    c: Coincident(g2,g3)
    c: Coincident(g3,g0)
    c: Symmetric(g0,g0,g-2)
    c: Symmetric(g1,g2,g-2)
FEATURE [PartDesign::Pocket] Pocket
  BaseFeature = -> Pad007
  Direction = (0,0,-1)
  Length = 5
  Length2 = 5
  Profile = -> Sketch008
  ReferenceAxis = -> Sketch008 [N_Axis]
  Refine = true
  Suppressed = false
  Type = 1
FEATURE [PartDesign::Body] Body
  AllowCompound = false
  Group = -> [Sketch,Pad,Sketch001,Pad001,Sketch002,Pad002,DatumPlane,Sketch003,Pad003,Sketch004,Pad004,Sketch005,Pad005,Sketch006,Pad006,Sketch007,Pad007,Sketch008,Pocket]
  Origin = -> Origin
  Tip = -> Pocket
FEATURE [Part::FeaturePython] Clone  label="tvboard_clone"  # Draft clone (typed FeaturePython)
  AttacherType = Attacher::AttachEngine3D
  Fuse = false
  Objects = -> [Body]
  Scale = (1,1,1)
FEATURE [App::Part] Part  label="tvboard"
  Group = -> [Clone]
  Origin = -> Origin001
COMPONENT P21 — geometry summary ("wachingmachine"; no construction recipe available for this part):
  bounding box: 920.0 x 780.0 x 440.0 mm
  tessellated surface: 3,706 triangles
  volume: 292547046 mm^3 (93% of its bounding box)
COMPONENT P22 — recipe-attached ("wall1500", a linked part whose construction recipe lives in a companion FreeCAD document of the same project; that document's serialized recipe follows).
Construction recipe (the companion document, serialized — sketch geometry with constraints, then the solid features built on it; lengths are millimeters unless a unit is written):

FCSTD DOCUMENT  (FreeCAD 1.0R39109 (Git))
Label: wall1500
License: All rights reserved
LicenseURL: https://en.wikipedia.org/wiki/All_rights_reserved
objects: Sketcher::SketchObject×1, PartDesign::Pad×1, PartDesign::Body×1, Part::FeaturePython×1, App::Part×1
note: 7 computed .brp shape members not serialized (recipe doc carries the construction recipe); baked Part::Feature solids carry a one-line shape summary decoded from their .brp

FEATURE [Sketcher::SketchObject] Sketch
  ArcFitTolerance = 1e-06
  AttachmentSupport = -> [XY_Plane]
  FullyConstrained = true
  MakeInternals = false
  MapMode = 5
  sketch-geometry (5):
    g0: LineSegment StartX=-750 StartY=-50 StartZ=0 EndX=750 EndY=-50 EndZ=0
    g1: LineSegment StartX=750 StartY=-50 StartZ=0 EndX=750 EndY=50 EndZ=0
    g2: LineSegment StartX=750 StartY=50 StartZ=0 EndX=-750 EndY=50 EndZ=0
    g3: LineSegment StartX=-750 StartY=50 StartZ=0 EndX=-750 EndY=-50 EndZ=0
    g4: GeomPoint [constr] X=0 Y=0 Z=0
  constraints (12):
    c: Coincident(g0,g1)
    c: Coincident(g1,g2)
    c: Coincident(g2,g3)
    c: Coincident(g3,g0)
    c: Horizontal(g0)
    c: Horizontal(g2)
    c: Vertical(g1)
    c: Vertical(g3)
    c: Symmetric(g2,g0,g4)
    c: Distance(g1,g3) = 1500
    c: Distance(g0,g2) = 100
    c: Coincident(g4,g-1)
FEATURE [PartDesign::Pad] Pad
  Direction = (0,0,1)
  Length = 3000
  Length2 = 10
  Profile = -> Sketch
  ReferenceAxis = -> Sketch [N_Axis]
  Refine = true
  Suppressed = false
  Type = 0
FEATURE [PartDesign::Body] Body
  AllowCompound = false
  Group = -> [Sketch,Pad]
  Origin = -> Origin
  Tip = -> Pad
FEATURE [Part::FeaturePython] Clone  label="wall1500_clone"  # Draft clone (typed FeaturePython)
  AttacherType = Attacher::AttachEngine3D
  Fuse = false
  Objects = -> [Body]
  Scale = (1,1,1)
FEATURE [App::Part] Part  label="wall1500"
  Group = -> [Clone]
  Origin = -> Origin001
COMPONENT P23 — same part as P22; its construction recipe is shown at P22.
PROVENANCE & LICENSES
A FreeCAD (.FCStd) document from a public repository crawl; recipes are the document's own serialized feature recipes (and, for linked parts, companion documents' recipes).
License: as declared in the source repository (recorded in the dataset sidecar).
